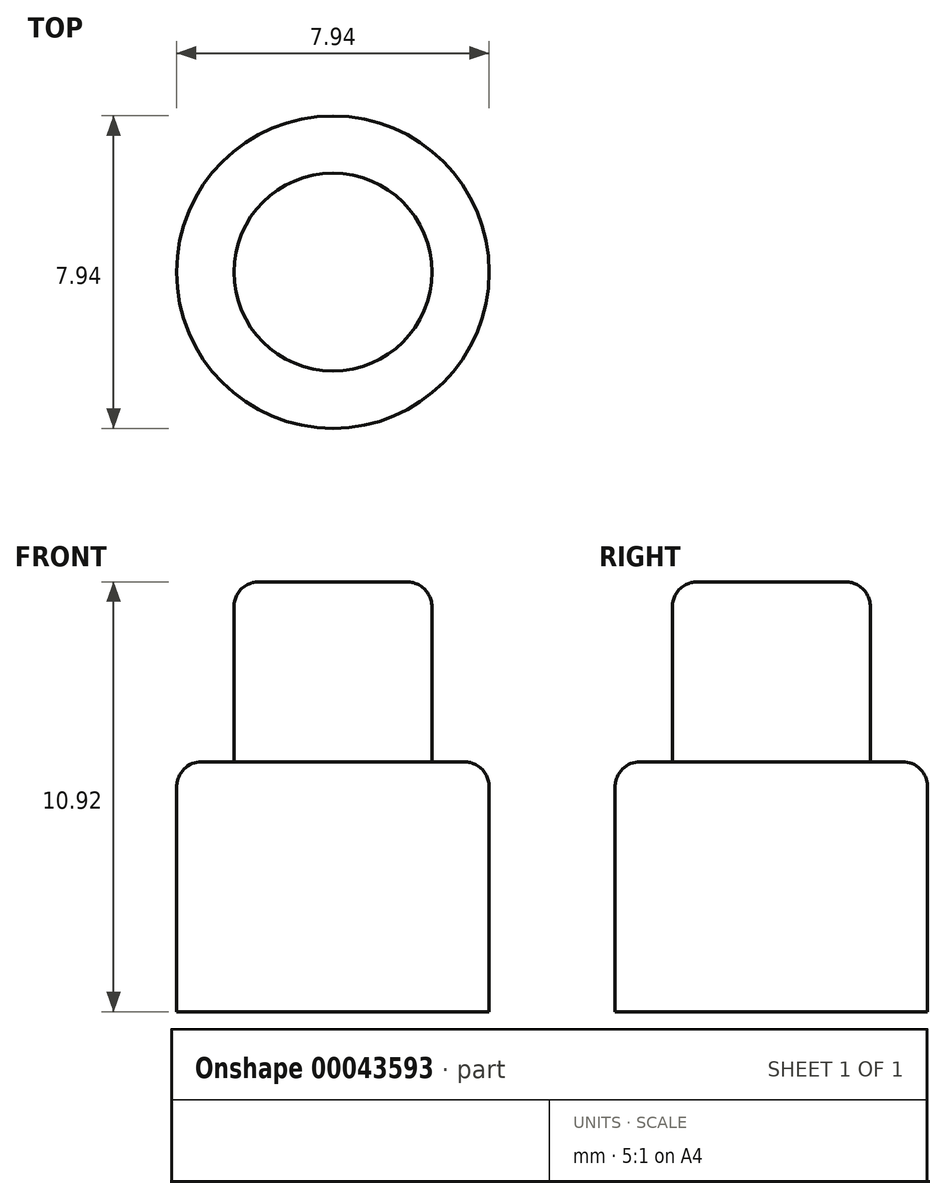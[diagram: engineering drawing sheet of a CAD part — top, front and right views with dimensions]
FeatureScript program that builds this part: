
annotation { "Feature Type Name" : "Feature", "Feature Type Description" : "" }
export const myFeature = defineFeature(function(context is Context, id is Id, definition is map)
    precondition{}
    {
        {
            var Q0;
            Q0=qCreatedBy(makeId("Top.planeOp"),FACE);
            var sketch = newSketch(context, id + "F0", { "sketchPlane" : qUnion([Q0])});
            skCircle(sketch, "E0", {"center": v(0, 0) * mm, "radius": 3.97 * mm});
            skSolve(sketch);
        }
        {
            var Q0;
            Q0 = qSketchRegion(id + "F0", true);
            extrude(context, id + "F1", {"entities" : qUnion([Q0]), "offsetDistance" : 25.4 * mm, "depth" : 6.35 * mm});
        }
        {
            var Q0;
            Q0=makeQuery(id+"F1.opExtrude","CAP_FACE",FACE,{"disambiguationData":[OSD([sQuery(id+"F0.wireOp",EDGE,"E0")])],"isStart":false});
            var sketch = newSketch(context, id + "F2", { "sketchPlane" : qUnion([Q0])});
            skCircle(sketch, "E1", {"center": v(0, 0) * mm, "radius": 2.51 * mm});
            skSolve(sketch);
        }
        {
            var Q0;
            Q0 = qSketchRegion(id + "F2", true);
            extrude(context, id + "F3", {"entities" : qUnion([Q0]), "operationType" : NewBodyOperationType.ADD, "depth" : 4.57 * mm});
        }
        {
            var Q0;
            Q0=makeQuery(id+"F3.opExtrude","CAP_FACE",FACE,{"disambiguationData":[OSD([sQuery(id+"F2.wireOp",EDGE,"E1")])],"isStart":false});
            var Q1;
            Q1=makeQuery(id+"F3.opExtrude","CAP_EDGE",EDGE,{"disambiguationData":[OSD([sQuery(id+"F2.wireOp",EDGE,"E1")])],"isStart":false});
            var Q2;
            Q2=makeQuery(id+"F1.opExtrude","CAP_EDGE",EDGE,{"disambiguationData":[OSD([sQuery(id+"F0.wireOp",EDGE,"E0")])],"isStart":false});
            fillet(context, id + "F4", {"entities" : qUnion([Q0, Q1, Q2]), "radius" : 0.64 * mm, "tangentPropagation" : true, "allowEdgeOverflow" : false});
        }
    });
